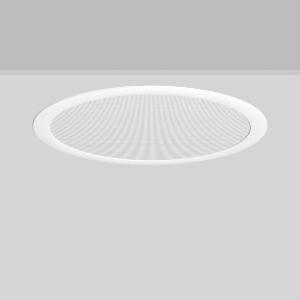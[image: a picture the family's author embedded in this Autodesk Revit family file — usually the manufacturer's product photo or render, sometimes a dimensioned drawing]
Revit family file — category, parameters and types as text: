
# Revit family: toledo_flat_pro_e_901719_002_2_730_b2dd
name_source: partatom
category: Lighting Fixtures
units: mm (PartAtom-declared; Revit-internal decimal feet)

## family parameters
Cut with Voids When Loaded = No
Host = Face
Light Source = No
Part Type = Normal
Room Calculation Point = No
Round Connector Dimension = Use Diameter
Shared = No

## types (1)
- TuneableWhite 946 (1 x LED Modul 946, 2700 lm, 4600)
    Apparent Load = 30 VA
    CIE Flux Codes = 65 90 98 100 100
    Color Rendering = 92
    Color Temperature = 4600
    Default Elevation = 1800 mm
    Description = Series: TOLEDO FLAT pro
Super-flat recessed downlight for high requirements. Housing: die-cast aluminium. Diffuser made from resistant polycarbonate (PC) with smooth surface on room side for low sensitivity to dirt and for the prevention of the accumulation of germs and bacteria. Satinised microprismatic diffuser prevents direct glare. Tunable white dynamically adjustable from 2700 K to 6500 K. Ceiling installation with spring system. Mounting depth depends on ceiling strength. Suitable for through-wiring. Including separate LED converter with connecting cable 250 mm. With Casambi smart+free Bluetooth control for wireless network and operation using Android / iOS devices, free app available for download. 
Colour: white
Diameter: 495 mm
Height: 6 mm
Cut-out diameter: 470 mm
Recess height: 55-75 mm
Luminaire: recess height: 31-51 mm
Lamp: LED
Socket: without socket
Colour temperature: 2700K - 6500K
Colour rendering index (CRI): 90
System power: 30 W
Rated luminous flux: 2700 lm
Luminous efficiency: 90 lm/W
System power 2: 30 W
Rated luminous flux 2: 2600 lm
Luminous efficiency 2: 87 lm/W
System power 3: 30 W
Rated luminous flux 3: 2500 lm
Luminous efficiency 3: 83 lm/W
Control gear: Dimmable Bluetooth converter
Protection class: II
Type of protection: IP 54
    Height = 0 mm  [stored 0 ft]
    Lamp = 1 x LED Modul 946
    Lamp Light Flux = 2700 lm
    Lamp count = 1
    Length = 495 mm
    Lifetime = 50000 h
    Luminous efficacy = 90 lm/W
    Manufacturer = RZB
    ModVariant = No
    Model = 901719.002.2.730
    Mounting Place = Ceiling
    Mounting Type = Recessed
    Number of Poles = 1
    OnlyDefault = Yes
    Power Factor = 1
    Product Name = TOLEDO FLAT pro E
    Product group = Recessed downlights
    ProductGroupID = 402
    Protection Class = Protection class II
    Protection Degree = Degree of protection
    RLX_Detail_Level = 1
    RLX_Emergency_Light_Flux = 0 lm
    RLX_Emergency_Type = 0
    RLX_Emergency_Type_DB = No
    RlxData = <blob elided: 39809 chars, md5=7a05a0e9>
    Socket = socket
    Standby Power = 0 W
    System Light Flux = 2700 lm
    System Power = 30 W
    Type Comments = TuneableWhite 946
    Type Image = 901719.002.76.jpg
    URL = http://relux.com
    VarID = tuneablewhite_946
    Voltage = 0 V
    Weight = 0.00 kg
    Width = 0 mm  [stored 0 ft]

note: [stored X ft] marks values corroborated as IEEE doubles in the binary element streams (Revit-internal decimal feet)

## geometry (parser evidence)
native form markers: Blend x4, Sweep x8
no freeform markers — native parametric forms only
